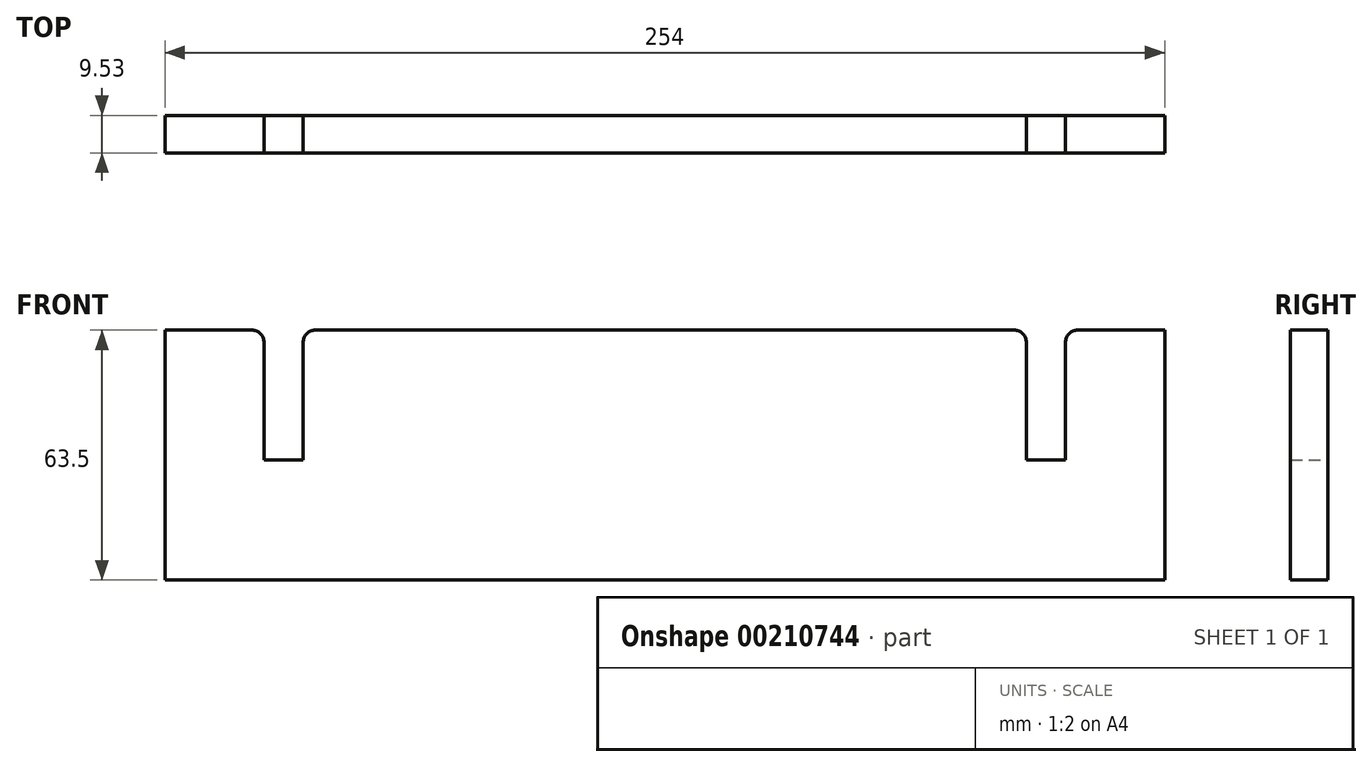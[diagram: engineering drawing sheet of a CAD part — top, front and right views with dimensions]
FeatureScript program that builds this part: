
annotation { "Feature Type Name" : "Feature", "Feature Type Description" : "" }
export const myFeature = defineFeature(function(context is Context, id is Id, definition is map)
    precondition{}
    {
        {
            var Q0;
            Q0=qCreatedBy(makeId("Front.planeOp"),FACE);
            var sketch = newSketch(context, id + "F0", { "sketchPlane" : qUnion([Q0])});
            skLineSegment(sketch, "E0", {"start": v(-110.97, 0) * mm, "end": v(-110.97, -63.5) * mm});
            skLineSegment(sketch, "E1", {"start": v(-110.97, -63.5) * mm, "end": v(143.03, -63.5) * mm});
            skLineSegment(sketch, "E2", {"start": v(143.03, -63.5) * mm, "end": v(143.03, 0) * mm});
            skLineSegment(sketch, "E3", {"start": v(143.03, 0) * mm, "end": v(121, 0) * mm});
            skLineSegment(sketch, "E4", {"start": v(117.82, -3.18) * mm, "end": v(117.82, -33.04) * mm});
            skLineSegment(sketch, "E5", {"start": v(117.82, -33.04) * mm, "end": v(107.91, -33.04) * mm});
            skLineSegment(sketch, "E6", {"start": v(107.91, -33.04) * mm, "end": v(107.91, -3.18) * mm});
            skLineSegment(sketch, "E7", {"start": v(104.74, 0) * mm, "end": v(-72.68, 0) * mm});
            skLineSegment(sketch, "E8", {"start": v(-75.85, -3.18) * mm, "end": v(-75.85, -33.04) * mm});
            skLineSegment(sketch, "E9", {"start": v(-75.85, -33.04) * mm, "end": v(-85.76, -33.04) * mm});
            skLineSegment(sketch, "E10", {"start": v(-85.76, -33.04) * mm, "end": v(-85.76, -3.18) * mm});
            skLineSegment(sketch, "E11", {"start": v(-88.94, 0) * mm, "end": v(-110.97, 0) * mm});
            skPoint(sketch, "E12.visualSharp", {"position": v(117.82, 0) * mm});
            skArc(sketch, "E12.filletArc", {"start": v(121, 0) * mm, "mid": v(118.75, -0.93) * mm, "end": v(117.82, -3.18) * mm});
            skPoint(sketch, "E13.visualSharp", {"position": v(107.91, 0) * mm});
            skArc(sketch, "E13.filletArc", {"start": v(107.91, -3.18) * mm, "mid": v(106.98, -0.93) * mm, "end": v(104.74, 0) * mm});
            skPoint(sketch, "E14.visualSharp", {"position": v(-75.85, 0) * mm});
            skArc(sketch, "E14.filletArc", {"start": v(-72.68, 0) * mm, "mid": v(-74.92, -0.93) * mm, "end": v(-75.85, -3.18) * mm});
            skPoint(sketch, "E15.visualSharp", {"position": v(-85.76, 0) * mm});
            skArc(sketch, "E15.filletArc", {"start": v(-85.76, -3.18) * mm, "mid": v(-86.7, -0.93) * mm, "end": v(-88.94, 0) * mm});
            skSolve(sketch);
        }
        {
            var Q0;
            Q0 = qSketchRegion(id + "F0", true);
            extrude(context, id + "F1", {"entities" : qUnion([Q0]), "depth" : 9.52 * mm});
        }
    });
